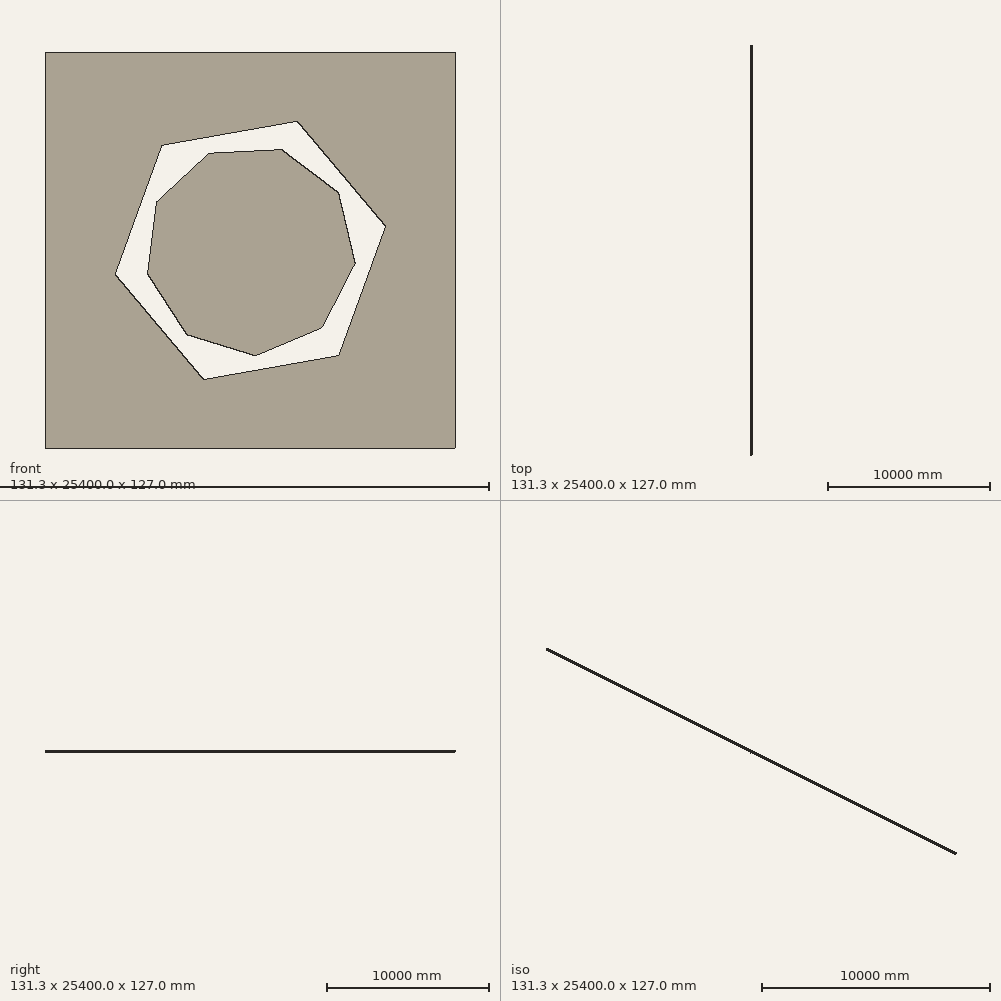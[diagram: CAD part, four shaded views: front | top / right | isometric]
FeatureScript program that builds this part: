
annotation { "Feature Type Name" : "Feature", "Feature Type Description" : "" }
export const myFeature = defineFeature(function(context is Context, id is Id, definition is map)
    precondition{}
    {
        {
            var Q0;
            Q0=qCreatedBy(makeId("Front.planeOp"),FACE);
            var sketch = newSketch(context, id + "F0", { "sketchPlane" : qUnion([Q0])});
            skPoint(sketch, "E0.first.point", {"position": v(0, 0) * mm});
            skCircle(sketch, "E1", {"center": v(0, 0) * mm, "radius": 63.5 * mm});
            skLineSegment(sketch, "E2.0", {"start": v(22.98, -24.77) * mm, "end": v(1.69, -33.75) * mm});
            skLineSegment(sketch, "E2.1", {"start": v(1.69, -33.75) * mm, "end": v(-20.4, -26.94) * mm});
            skLineSegment(sketch, "E2.2", {"start": v(-20.4, -26.94) * mm, "end": v(-32.94, -7.52) * mm});
            skLineSegment(sketch, "E2.3", {"start": v(-32.94, -7.52) * mm, "end": v(-30.07, 15.41) * mm});
            skLineSegment(sketch, "E2.4", {"start": v(-30.07, 15.41) * mm, "end": v(-13.13, 31.13) * mm});
            skLineSegment(sketch, "E2.5", {"start": v(-13.13, 31.13) * mm, "end": v(9.95, 32.29) * mm});
            skLineSegment(sketch, "E2.6", {"start": v(9.95, 32.29) * mm, "end": v(28.18, 18.49) * mm});
            skLineSegment(sketch, "E2.7", {"start": v(28.18, 18.49) * mm, "end": v(33.53, -4.2) * mm});
            skLineSegment(sketch, "E2.8", {"start": v(33.53, -4.2) * mm, "end": v(22.98, -24.77) * mm});
            skPoint(sketch, "E2.0.midPoint", {"position": v(12.34, -29.26) * mm});
            skArc(sketch, "E3", {"start": v(-75.95, -75.59) * mm, "mid": v(38.2, -119.75) * mm, "end": v(63.5, 0) * mm});
            skLineSegment(sketch, "E4.bottom", {"start": v(65.63, 63.5) * mm, "end": v(-65.63, 63.5) * mm});
            skLineSegment(sketch, "E4.top", {"start": v(65.63, -63.5) * mm, "end": v(-65.63, -63.5) * mm});
            skLineSegment(sketch, "E4.left", {"start": v(65.63, 63.5) * mm, "end": v(65.63, -63.5) * mm});
            skLineSegment(sketch, "E4.right", {"start": v(-65.63, 63.5) * mm, "end": v(-65.63, -63.5) * mm});
            skCircle(sketch, "E5.cCircle", {"center": v(0, 0) * mm, "radius": 38.1 * mm, "construction": true});
            skLineSegment(sketch, "E5.0", {"start": v(-28.32, 33.67) * mm, "end": v(15, 41.36) * mm});
            skLineSegment(sketch, "E5.1", {"start": v(15, 41.36) * mm, "end": v(43.32, 7.7) * mm});
            skLineSegment(sketch, "E5.2", {"start": v(43.32, 7.7) * mm, "end": v(28.32, -33.67) * mm});
            skLineSegment(sketch, "E5.3", {"start": v(28.32, -33.67) * mm, "end": v(-15, -41.36) * mm});
            skLineSegment(sketch, "E5.4", {"start": v(-15, -41.36) * mm, "end": v(-43.32, -7.7) * mm});
            skLineSegment(sketch, "E5.5", {"start": v(-43.32, -7.7) * mm, "end": v(-28.32, 33.67) * mm});
            skPoint(sketch, "E5.0.midPoint", {"position": v(-6.66, 37.51) * mm});
            skSolve(sketch);
        }
        {
            var Q0;
            Q0=makeQuery(id+"F0.imprint","IMPRINT",FACE,{"disambiguationData":[TD([[makeQuery(id+"F0.imprint","IMPRINT",EDGE,{"derivedFrom":sQuery(id+"F0.wireOp",EDGE,"E2.0")}),-1.0]])]});
            extrude(context, id + "F1", {"entities" : qUnion([Q0]), "endBound" : BoundingType.SYMMETRIC, "depth" : 25400 * mm});
        }
        {
            var Q0;
            Q0 = qSketchRegion(id + "F0", true);
            extrude(context, id + "F2", {"entities" : qUnion([Q0]), "endBound" : BoundingType.SYMMETRIC, "depth" : 0.03 * mm});
        }
    });
